# Revit family: LEL
name_source: partatom
category: Lighting Fixtures
units: mm (PartAtom-declared; Revit-internal decimal feet)

## family parameters
Always vertical = Yes
Cut with Voids When Loaded = No
Host = Ceiling
Light Source = Yes
OmniClass Number = 23.80.70.11.14.11
OmniClass Title = Downlights
Part Type = Normal
Room Calculation Point = No
Round Connector Dimension = Use Diameter
Shared = No

## types (6) — shared parameters
Assembly Code = D5020200
Color Filter = 16777215
Description = Premium-grade, LED Ellipse strip luminaire
Dimming Lamp Color Temperature Shift = <None>
Housing Finish = Metal - Viscor - White
Lamp = LED
Lens Finish = Acrylic - Viscor - Frosted Round
Manufacturer = VISIONEERING by VISCOR
Model = LEL
Tilt Angle = 90.00°
URL = https://www.viscor.com
Voltage = 120 V
Width = 0' - 5 17/32"

## per-type parameters (varying)
| type | Apparent Load | Emit from Line Length | Lamp Wattage | Length | Photometric Web File |
| LEL24-LED840K020LUNV | 16 VA | 1' - 11 3/32" | 16 VA | 1' - 11 3/32" | LEL24-LED840K020LUNV-G002178.IES |
| LEL24-LED840K041LUNV | 32 VA | 1' - 11 3/32" | 32 VA | 1' - 11 3/32" | LEL24-LED840K041LUNV-G002175.IES |
| LEL48-LED840K020LUNV | 15 VA | 3' - 9 3/32" | 15 VA | 3' - 9 3/32" | LEL48-LED840K020LUNV-G002197.IES |
| LEL48-LED840K041LUNV | 32 VA | 3' - 9 3/32" | 32 VA | 3' - 9 3/32" | LEL48-LED840K041LUNV-G002194.IES |
| LEL48-LED840K053LUNV | 39 VA | 3' - 9 3/32" | 39 VA | 3' - 9 3/32" | LEL48-LED840K053LUNV-G003486.IES |
| LEL48-LED840K082LUNV | 64 VA | 3' - 9 3/32" | 64 VA | 3' - 9 3/32" | LEL48-LED840K082LUNV-G002186.IES |

## geometry (parser evidence)
native form markers: Sweep x3
no freeform markers — native parametric forms only
